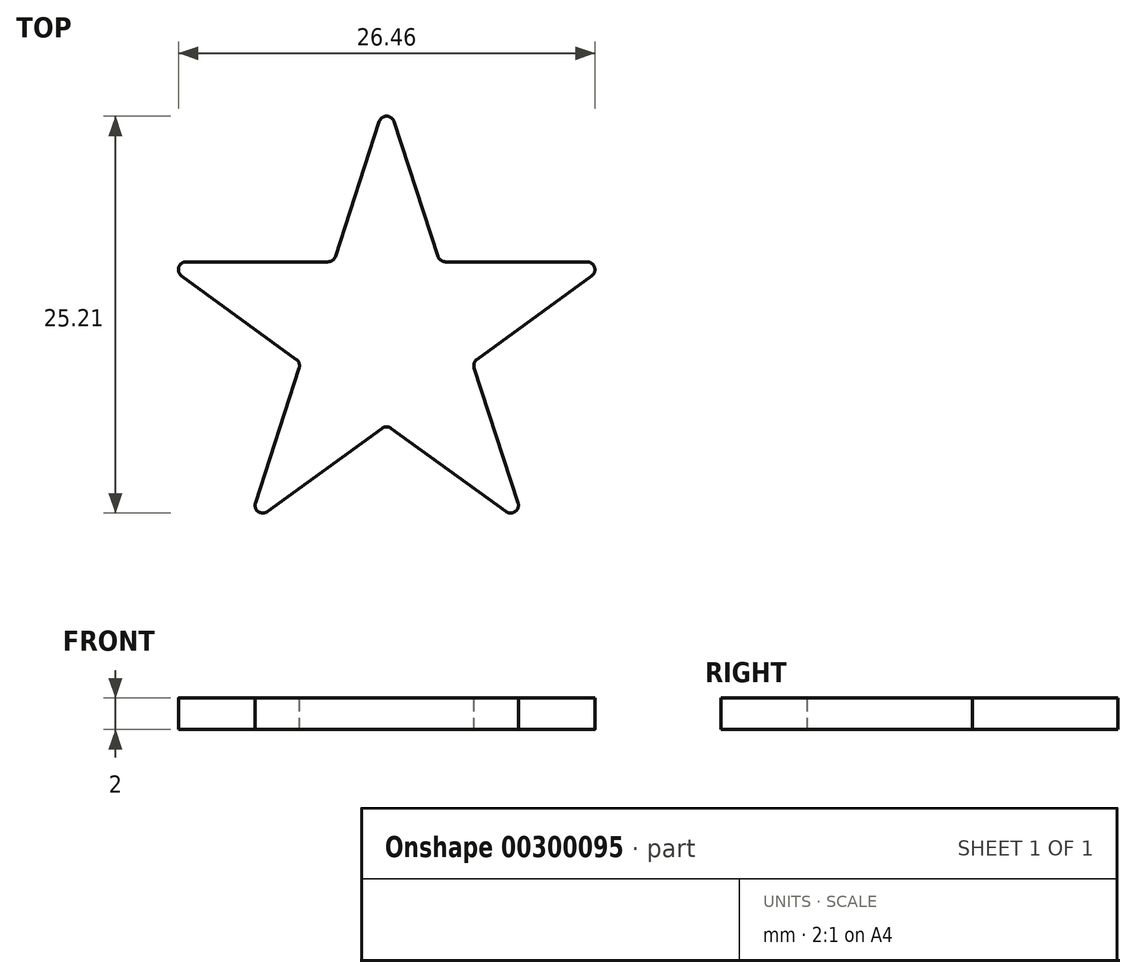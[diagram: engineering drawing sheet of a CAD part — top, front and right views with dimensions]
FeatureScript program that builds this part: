
annotation { "Feature Type Name" : "Feature", "Feature Type Description" : "" }
export const myFeature = defineFeature(function(context is Context, id is Id, definition is map)
    precondition{}
    {
        {
            var Q0;
            Q0=qCreatedBy(makeId("Top.planeOp"),FACE);
            var sketch = newSketch(context, id + "F0", { "sketchPlane" : qUnion([Q0])});
            skCircle(sketch, "E0.cCircle", {"center": v(0, 0) * mm, "radius": 15 * mm, "construction": true});
            skLineSegment(sketch, "E0.0", {"start": v(0, 15) * mm, "end": v(14.27, 4.64) * mm, "construction": true});
            skLineSegment(sketch, "E0.1", {"start": v(14.27, 4.64) * mm, "end": v(8.82, -12.14) * mm, "construction": true});
            skLineSegment(sketch, "E0.2", {"start": v(8.82, -12.14) * mm, "end": v(-8.82, -12.14) * mm, "construction": true});
            skLineSegment(sketch, "E0.3", {"start": v(-8.82, -12.14) * mm, "end": v(-14.27, 4.64) * mm, "construction": true});
            skLineSegment(sketch, "E0.4", {"start": v(-14.27, 4.64) * mm, "end": v(0, 15) * mm, "construction": true});
            skLineSegment(sketch, "E1", {"start": v(0, 15) * mm, "end": v(-3.37, 4.64) * mm});
            skLineSegment(sketch, "E2", {"start": v(-8.82, -12.14) * mm, "end": v(0, -5.73) * mm});
            skLineSegment(sketch, "E3", {"start": v(-14.27, 4.64) * mm, "end": v(-3.37, 4.64) * mm});
            skLineSegment(sketch, "E4", {"start": v(8.82, -12.14) * mm, "end": v(5.45, -1.77) * mm});
            skLineSegment(sketch, "E5", {"start": v(-14.27, 4.64) * mm, "end": v(-5.45, -1.77) * mm});
            skLineSegment(sketch, "E6.trimOffspring", {"start": v(3.37, 4.64) * mm, "end": v(14.27, 4.64) * mm});
            skLineSegment(sketch, "E7.trimOffspring", {"start": v(-5.45, -1.77) * mm, "end": v(-8.82, -12.14) * mm});
            skLineSegment(sketch, "E8.trimOffspring", {"start": v(0, -5.73) * mm, "end": v(8.82, -12.14) * mm});
            skLineSegment(sketch, "E9.trimOffspring", {"start": v(5.45, -1.77) * mm, "end": v(14.27, 4.64) * mm});
            skLineSegment(sketch, "E10.trimOffspring", {"start": v(3.37, 4.64) * mm, "end": v(0, 15) * mm});
            skSolve(sketch);
        }
        {
            var Q0;
            Q0=makeQuery(id+"F0.imprint","IMPRINT",FACE,{"disambiguationData":[TD([[makeQuery(id+"F0.imprint","IMPRINT",EDGE,{"derivedFrom":sQuery(id+"F0.wireOp",EDGE,"E1")}),1.0]])]});
            extrude(context, id + "F1", {"entities" : qUnion([Q0]), "depth" : 2 * mm});
        }
        {
            var Q0;
            Q0=makeQuery(id+"F1.opExtrude","SWEPT_EDGE",EDGE,{"disambiguationData":[OSD([sQuery(id+"F0.wireOp",EDGE,"E1"),sQuery(id+"F0.wireOp",EDGE,"E10.trimOffspring")])]});
            var Q1;
            Q1=makeQuery(id+"F1.opExtrude","SWEPT_EDGE",EDGE,{"disambiguationData":[OSD([sQuery(id+"F0.wireOp",EDGE,"E3"),sQuery(id+"F0.wireOp",EDGE,"E5")])]});
            var Q2;
            Q2=makeQuery(id+"F1.opExtrude","SWEPT_EDGE",EDGE,{"disambiguationData":[OSD([sQuery(id+"F0.wireOp",EDGE,"E6.trimOffspring"),sQuery(id+"F0.wireOp",EDGE,"E9.trimOffspring")])]});
            var Q3;
            Q3=makeQuery(id+"F1.opExtrude","SWEPT_EDGE",EDGE,{"disambiguationData":[OSD([sQuery(id+"F0.wireOp",EDGE,"E4"),sQuery(id+"F0.wireOp",EDGE,"E8.trimOffspring")])]});
            var Q4;
            Q4=makeQuery(id+"F1.opExtrude","SWEPT_EDGE",EDGE,{"disambiguationData":[OSD([sQuery(id+"F0.wireOp",EDGE,"E2"),sQuery(id+"F0.wireOp",EDGE,"E7.trimOffspring")])]});
            fillet(context, id + "F2", {"entities" : qUnion([Q0, Q1, Q2, Q3, Q4]), "radius" : 0.5 * mm, "tangentPropagation" : true, "allowEdgeOverflow" : false});
        }
        {
            var Q0;
            Q0=makeQuery(id+"F1.opExtrude","SWEPT_EDGE",EDGE,{"disambiguationData":[OSD([sQuery(id+"F0.wireOp",EDGE,"E2"),sQuery(id+"F0.wireOp",EDGE,"E8.trimOffspring")])]});
            var Q1;
            Q1=makeQuery(id+"F1.opExtrude","SWEPT_EDGE",EDGE,{"disambiguationData":[OSD([sQuery(id+"F0.wireOp",EDGE,"E4"),sQuery(id+"F0.wireOp",EDGE,"E9.trimOffspring")])]});
            var Q2;
            Q2=makeQuery(id+"F1.opExtrude","SWEPT_EDGE",EDGE,{"disambiguationData":[OSD([sQuery(id+"F0.wireOp",EDGE,"E6.trimOffspring"),sQuery(id+"F0.wireOp",EDGE,"E10.trimOffspring")])]});
            var Q3;
            Q3=makeQuery(id+"F1.opExtrude","SWEPT_EDGE",EDGE,{"disambiguationData":[OSD([sQuery(id+"F0.wireOp",EDGE,"E1"),sQuery(id+"F0.wireOp",EDGE,"E3")])]});
            var Q4;
            Q4=makeQuery(id+"F1.opExtrude","SWEPT_EDGE",EDGE,{"disambiguationData":[OSD([sQuery(id+"F0.wireOp",EDGE,"E5"),sQuery(id+"F0.wireOp",EDGE,"E7.trimOffspring")])]});
            fillet(context, id + "F3", {"entities" : qUnion([Q0, Q1, Q2, Q3, Q4]), "radius" : 0.5 * mm, "tangentPropagation" : true, "allowEdgeOverflow" : false});
        }
    });
